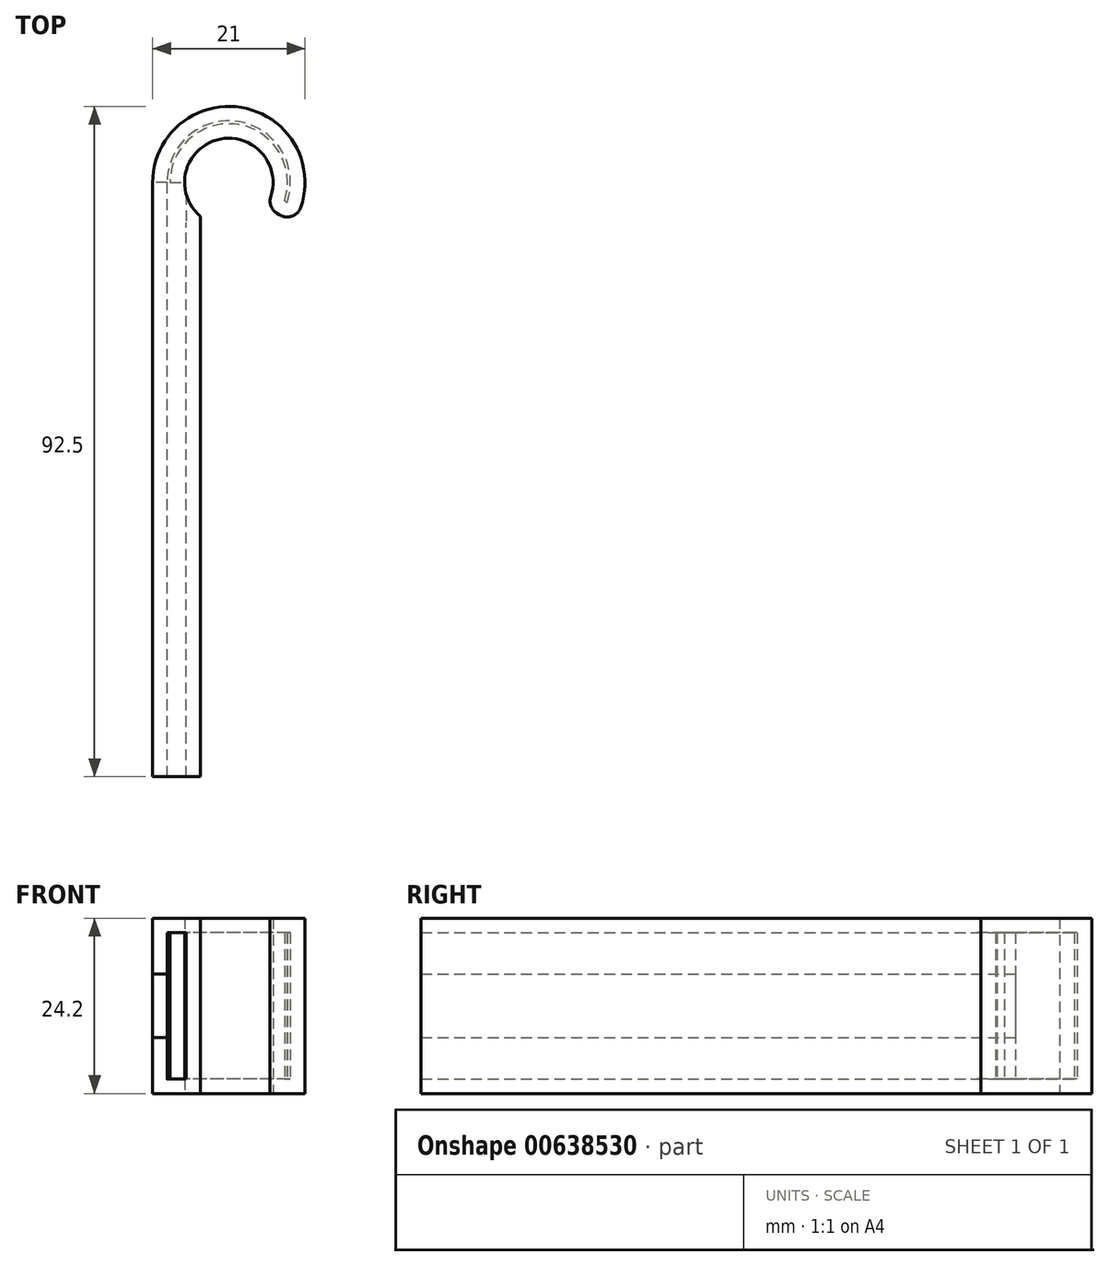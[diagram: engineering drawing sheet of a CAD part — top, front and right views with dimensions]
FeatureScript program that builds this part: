
annotation { "Feature Type Name" : "Feature", "Feature Type Description" : "" }
export const myFeature = defineFeature(function(context is Context, id is Id, definition is map)
    precondition{}
    {
        {
            var Q0;
            Q0=qCreatedBy(makeId("Top.planeOp"),FACE);
            var sketch = newSketch(context, id + "F0", { "sketchPlane" : qUnion([Q0])});
            skLineSegment(sketch, "E0", {"start": v(-14.57, -25.42) * mm, "end": v(-14.57, 56.58) * mm});
            skLineSegment(sketch, "E1.0", {"start": v(-7.97, -25.42) * mm, "end": v(-7.97, 51.9) * mm});
            skLineSegment(sketch, "E2", {"start": v(-14.57, -25.42) * mm, "end": v(-7.97, -25.42) * mm});
            skCircle(sketch, "E3", {"center": v(-4.07, 56.58) * mm, "radius": 6.1 * mm});
            skLineSegment(sketch, "E4.0", {"start": v(-10.17, -25.42) * mm, "end": v(-10.17, 56.58) * mm});
            skCircle(sketch, "E5.0", {"center": v(-4.07, 56.58) * mm, "radius": 10.5 * mm});
            skLineSegment(sketch, "E6", {"start": v(4.78, 50.94) * mm, "end": v(1.06, 53.28) * mm});
            skLineSegment(sketch, "E7.0", {"start": v(-12.37, -25.42) * mm, "end": v(-12.37, 56.58) * mm});
            skSolve(sketch);
        }
        {
            var Q0;
            {var subQ2=sQuery(id+"F0.wireOp",EDGE,"E6");Q0=makeQuery(id+"F0.imprint","IMPRINT",FACE,{"disambiguationData":[TD([[makeQuery(id+"F0.imprint","IMPRINT",EDGE,{"derivedFrom":subQ2}),-1.0]])]});}
            var Q1;
            {var subQ0=sQuery(id+"F0.wireOp",EDGE,"E0");Q1=makeQuery(id+"F0.imprint","IMPRINT",FACE,{"disambiguationData":[TD([[makeQuery(id+"F0.imprint","IMPRINT",EDGE,{"derivedFrom":subQ0}),-1.0]])]});}
            var Q2;
            {var subQ0=sQuery(id+"F0.wireOp",EDGE,"E2");var subQ1=sQuery(id+"F0.wireOp",EDGE,"E1.0");var subQ2=makeQuery(id+"F0.imprint","INTERSECT",VERTEX,{"derivedFrom":[subQ1,subQ0]});Q2=makeQuery(id+"F0.imprint","IMPRINT",FACE,{"disambiguationData":[TD([[makeQuery(id+"F0.imprint","IMPRINT",EDGE,{"disambiguationData":[TD([[subQ2,-1.0]])],"derivedFrom":subQ1}),1.0]])]});}
            var Q3;
            {var subQ0=sQuery(id+"F0.wireOp",EDGE,"E3");var subQ1=sQuery(id+"F0.wireOp",EDGE,"E1.0");var subQ2=makeQuery(id+"F0.imprint","INTERSECT",VERTEX,{"derivedFrom":[subQ1,subQ0]});Q3=makeQuery(id+"F0.imprint","IMPRINT",FACE,{"disambiguationData":[TD([[makeQuery(id+"F0.imprint","IMPRINT",EDGE,{"disambiguationData":[TD([[subQ2,1.0]])],"derivedFrom":subQ1}),1.0]])]});}
            var Q4;
            {var subQ0=sQuery(id+"F0.wireOp",EDGE,"E4.0");var subQ1=sQuery(id+"F0.wireOp",EDGE,"E2");var subQ2=makeQuery(id+"F0.imprint","INTERSECT",VERTEX,{"derivedFrom":[subQ1,subQ0]});Q4=makeQuery(id+"F0.imprint","IMPRINT",FACE,{"disambiguationData":[TD([[makeQuery(id+"F0.imprint","IMPRINT",EDGE,{"disambiguationData":[TD([[subQ2,1.0]])],"derivedFrom":subQ1}),1.0]])]});}
            extrude(context, id + "F1", {"entities" : qUnion([Q0, Q1, Q2, Q3, Q4]), "depth" : 24.2 * mm, "offsetDistance" : 25 * mm});
        }
        {
            var Q0;
            Q0=makeQuery(id+"F1.opExtrude","SWEPT_EDGE",EDGE,{"disambiguationData":[OSD([sQuery(id+"F0.wireOp",EDGE,"E3"),sQuery(id+"F0.wireOp",EDGE,"E6")])]});
            var Q1;
            Q1=makeQuery(id+"F1.opExtrude","SWEPT_EDGE",EDGE,{"disambiguationData":[OSD([sQuery(id+"F0.wireOp",EDGE,"E5.0"),sQuery(id+"F0.wireOp",EDGE,"E6")])]});
            fillet(context, id + "F2", {"entities" : qUnion([Q0, Q1]), "radius" : 2 * mm, "tangentPropagation" : true, "allowEdgeOverflow" : false});
        }
        {
            var Q0;
            Q0=makeQuery(id+"F1.opExtrude","SWEPT_FACE",FACE,{"disambiguationData":[OSD([sQuery(id+"F0.wireOp",EDGE,"E0")])]});
            var Q1;
            Q1=makeQuery(id+"F1.opExtrude","SWEPT_FACE",FACE,{"disambiguationData":[OSD([sQuery(id+"F0.wireOp",EDGE,"E2")])]});
            shell(context, id + "F3", {"entities" : qUnion([Q0, Q1]), "thickness" : 2 * mm});
        }
        {
            var Q0;
            {var subQ0=sQuery(id+"F0.wireOp",EDGE,"E6");var subQ1=sQuery(id+"F0.wireOp",EDGE,"E5.0");var subQ2=sQuery(id+"F0.wireOp",EDGE,"E3");var subQ3=sQuery(id+"F0.wireOp",EDGE,"E2");var subQ4=sQuery(id+"F0.wireOp",EDGE,"E1.0");var subQ5=sQuery(id+"F0.wireOp",EDGE,"E0");Q0=makeQuery(id+"F3.opShell","OFFSET_FACE",FACE,{"disambiguationData":[OSD([subQ5,subQ4,subQ3,subQ2,subQ1,subQ0]),TDD([makeQuery(id+"F1.opExtrude","CAP_FACE",FACE,{"disambiguationData":[OSD([subQ5,subQ4,subQ3,subQ2,subQ1,subQ0])],"isStart":true})])]});}
            var sketch = newSketch(context, id + "F4", { "sketchPlane" : qUnion([Q0])});
            skLineSegment(sketch, "E8.bottom", {"start": v(-14.57, -25.42) * mm, "end": v(-12.57, -25.42) * mm});
            skLineSegment(sketch, "E8.top", {"start": v(-14.57, 56.58) * mm, "end": v(-12.57, 56.58) * mm});
            skLineSegment(sketch, "E8.left", {"start": v(-14.57, -25.42) * mm, "end": v(-14.57, 56.58) * mm});
            skLineSegment(sketch, "E8.right", {"start": v(-12.57, -25.42) * mm, "end": v(-12.57, 56.58) * mm});
            skSolve(sketch);
        }
        {
            var Q0;
            Q0=makeQuery(id+"F4.imprint","IMPRINT",FACE,{"disambiguationData":[TD([[makeQuery(id+"F4.imprint","IMPRINT",EDGE,{"derivedFrom":sQuery(id+"F4.wireOp",EDGE,"E8.bottom")}),1.0]])]});
            extrude(context, id + "F5", {"entities" : qUnion([Q0]), "operationType" : NewBodyOperationType.ADD, "depth" : 5.7 * mm, "offsetDistance" : 25 * mm});
        }
        {
            var Q0;
            {var subQ0=sQuery(id+"F0.wireOp",EDGE,"E6");var subQ1=sQuery(id+"F0.wireOp",EDGE,"E5.0");var subQ2=sQuery(id+"F0.wireOp",EDGE,"E3");var subQ3=sQuery(id+"F0.wireOp",EDGE,"E2");var subQ4=sQuery(id+"F0.wireOp",EDGE,"E1.0");var subQ5=sQuery(id+"F0.wireOp",EDGE,"E0");Q0=makeQuery(id+"F3.opShell","OFFSET_FACE",FACE,{"disambiguationData":[OSD([subQ5,subQ4,subQ3,subQ2,subQ1,subQ0]),TDD([makeQuery(id+"F1.opExtrude","CAP_FACE",FACE,{"disambiguationData":[OSD([subQ5,subQ4,subQ3,subQ2,subQ1,subQ0])],"isStart":false})])]});}
            var sketch = newSketch(context, id + "F6", { "sketchPlane" : qUnion([Q0])});
            skLineSegment(sketch, "E9.bottom", {"start": v(-14.57, 25.42) * mm, "end": v(-12.57, 25.42) * mm});
            skLineSegment(sketch, "E9.top", {"start": v(-14.57, -56.58) * mm, "end": v(-12.57, -56.58) * mm});
            skLineSegment(sketch, "E9.left", {"start": v(-14.57, 25.42) * mm, "end": v(-14.57, -56.58) * mm});
            skLineSegment(sketch, "E9.right", {"start": v(-12.57, 25.42) * mm, "end": v(-12.57, -56.58) * mm});
            skSolve(sketch);
        }
        {
            var Q0;
            Q0=makeQuery(id+"F6.imprint","IMPRINT",FACE,{"disambiguationData":[TD([[makeQuery(id+"F6.imprint","IMPRINT",EDGE,{"derivedFrom":sQuery(id+"F6.wireOp",EDGE,"E9.bottom")}),-1.0]])]});
            extrude(context, id + "F7", {"entities" : qUnion([Q0]), "operationType" : NewBodyOperationType.ADD, "depth" : 5.7 * mm, "offsetDistance" : 25 * mm});
        }
        {
            var Q0;
            {var subQ0=sQuery(id+"F0.wireOp",EDGE,"E6");var subQ1=sQuery(id+"F0.wireOp",EDGE,"E5.0");var subQ2=sQuery(id+"F0.wireOp",EDGE,"E3");var subQ3=sQuery(id+"F0.wireOp",EDGE,"E2");var subQ4=sQuery(id+"F0.wireOp",EDGE,"E1.0");var subQ5=sQuery(id+"F0.wireOp",EDGE,"E0");Q0=makeQuery(id+"F3.opShell","OFFSET_FACE",FACE,{"disambiguationData":[OSD([subQ5,subQ4,subQ3,subQ2,subQ1,subQ0]),TDD([makeQuery(id+"F1.opExtrude","CAP_FACE",FACE,{"disambiguationData":[OSD([subQ5,subQ4,subQ3,subQ2,subQ1,subQ0])],"isStart":true})])]});}
            var sketch = newSketch(context, id + "F8", { "sketchPlane" : qUnion([Q0])});
            skLineSegment(sketch, "E10.bottom", {"start": v(-12.18, 56.58) * mm, "end": v(-9.98, 56.58) * mm});
            skLineSegment(sketch, "E10.top", {"start": v(-12.18, 50.38) * mm, "end": v(-9.98, 50.38) * mm});
            skLineSegment(sketch, "E10.left", {"start": v(-12.18, 56.58) * mm, "end": v(-12.18, 50.38) * mm});
            skLineSegment(sketch, "E10.right", {"start": v(-9.98, 56.58) * mm, "end": v(-9.98, 50.38) * mm});
            skSolve(sketch);
        }
        {
            var Q0;
            Q0 = qSketchRegion(id + "F8", true);
            extrude(context, id + "F9", {"entities" : qUnion([Q0]), "operationType" : NewBodyOperationType.REMOVE, "depth" : 20.2 * mm, "offsetDistance" : 25 * mm});
        }
    });
